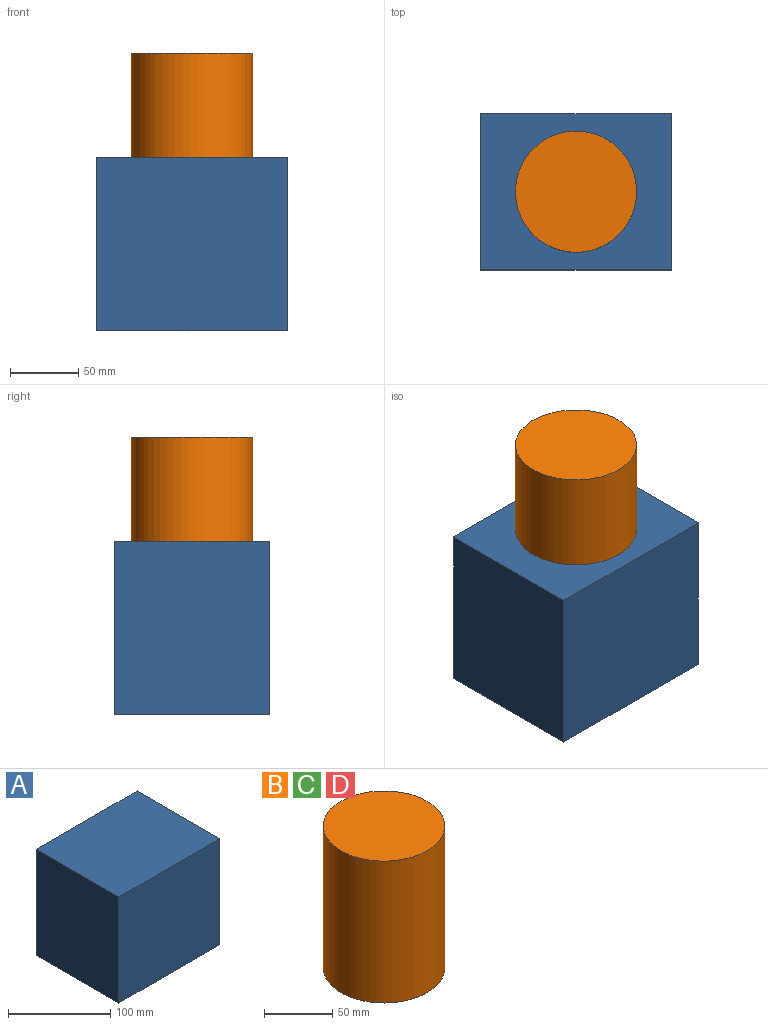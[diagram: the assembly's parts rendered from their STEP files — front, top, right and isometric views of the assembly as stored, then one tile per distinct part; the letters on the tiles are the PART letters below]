
ASSEMBLY  parts=4 mates=1
PART A: 8 faces, bbox 139.7x114.3x127 mm
  f0: plane 127x114.3mm, normal (1,0,0), area 14516.1mm2, adj f1,f3,f4,f5
  f1: plane 139.7x127mm, normal (0,1,0), area 17741.9mm2, adj f0,f2,f4,f5
  f2: plane 127x114.3mm, normal (-1,0,0), area 14516.1mm2, adj f1,f3,f4,f5
  f3: plane 139.7x127mm, normal (0,-1,0), area 17741.9mm2, adj f0,f2,f4,f5
  f4: plane 139.7x114.3mm, normal (0,0,1), area 15967.7mm2, adj f0,f1,f2,f3
  f5: plane 139.7x114.3mm, normal (0,0,-1), area 9760.5mm2, adj f0,f1,f2,f3,f6
  f6: cylinder r=44.45mm len=88.9mm, axis (0,0,-1), area 14187.8mm2, adj f5,f7
  f7: plane 88.9x88.9mm, normal (0,0,-1), area 6207.2mm2, adj f6
PART B: 3 faces, bbox 88.9x88.9x127 mm
  f0: cylinder r=44.45mm len=127mm, axis (0,0,-1), area 35469.5mm2, adj f1,f2
  f1: plane 88.9x88.9mm, normal (0,0,1), area 6207.2mm2, adj f0
  f2: plane 88.9x88.9mm, normal (0,0,-1), area 6207.2mm2, adj f0
PART C: same geometry as B
PART D: same geometry as B
PLACE A rot(axis=(1,0,0),180deg) t=(-12.87,-0.01,30.18)mm
PLACE B t=(-12.87,-0.01,-20.62)mm fixed
PLACE C t=(-12.87,-0.01,-20.62)mm fixed
PLACE D t=(-12.87,-0.01,-20.62)mm
MATE revolute A.f6 <-> C.f0  axis (0,0,1) through (-12.87,-0.01,-20.62)mm
